# Revit family: CB9R
name_source: partatom
category: Lighting Fixtures
revit_build: Autodesk Revit 2014 (Build: 20130308_1515(x64)
units: mm (PartAtom-declared; Revit-internal decimal feet)

## types (3) — shared parameters
Apparent Load = 0 VA
Assembly Code = D5020200
Body Material = Concrete-Hubbell- Sand/Cement Screed
Color Filter = 16777215
Default Elevation = 0"
Description = Architectural Outdoor Lighting
Dimming Lamp Color Temperature Shift = <None>
Emit Shape Visible in Rendering = No
Emit from Circle Diameter = 6"
Glass Material = Glass-Kim Lighting-Clear
Grille Length = 6"
Grille material = Paint - Hubbell - Carbon Black
Lamp = LED
Load Classification = Lighting
Manufacturer = Architectural Area Lighting
MasterFormat Title = Parking Lighting, Roadway Lighting, Site Lighting
Model = CB9R
Number of Poles = 1
OmniClass Number = 23.80.70.14.11.11
OmniClass Title = Lighting Bollard
Photometric Notes = More IES files download on Photometric Web Link
Photometric Web File = CB9R-CO-27LED-BW.IES
Photometric Web Link = https://www.hubbell.com
Power Factor = 1
Product Documentation Link = https://hubbellcdn.com
Product Page URL = https://www.hubbell.com
Series = Concrete Bollard
Tilt Angle = 90.00°
Type Comments = Lighting Fixture
URL = https://www.hubbell.com
Voltage = 120 V
Wattage Comments = 28W

## type names (no varying parameters)
- 24"
- 36"
- 42"

note: column(s) folded — value = type name in every type: Shaft Height

## geometry (parser evidence)
native form markers: Blend x12, Sweep x2
no freeform markers — native parametric forms only
